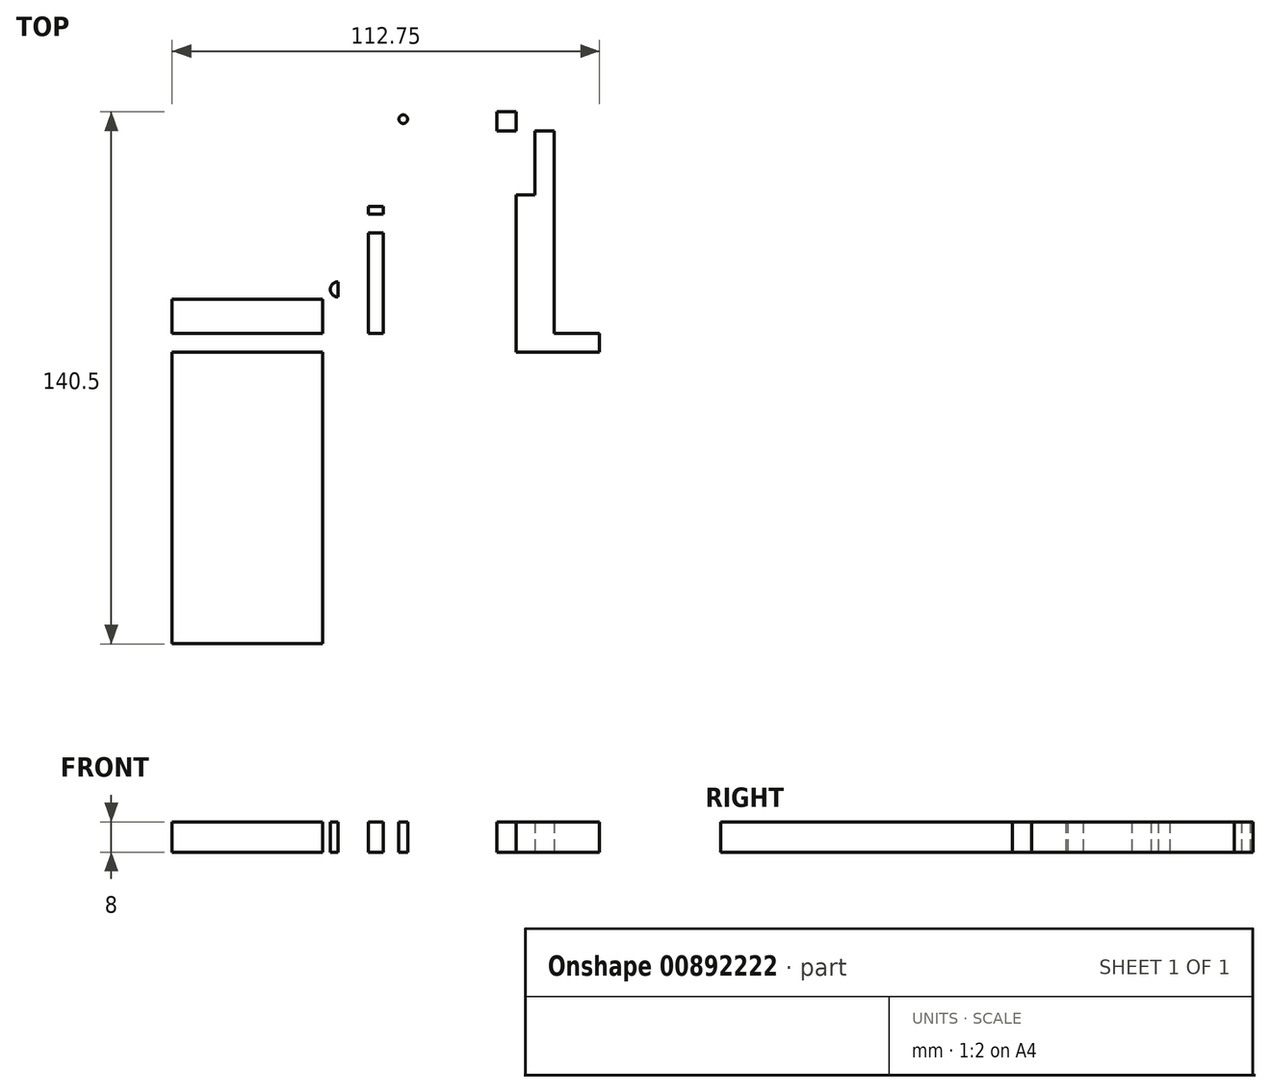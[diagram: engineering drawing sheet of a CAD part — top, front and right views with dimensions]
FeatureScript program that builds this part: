
annotation { "Feature Type Name" : "Feature", "Feature Type Description" : "" }
export const myFeature = defineFeature(function(context is Context, id is Id, definition is map)
    precondition{}
    {
        {
            var Q0;
            Q0=qCreatedBy(makeId("Top.planeOp"),FACE);
            var sketch = newSketch(context, id + "F0", { "sketchPlane" : qUnion([Q0])});
            skLineSegment(sketch, "E0.bottom", {"start": v(-40.7, -58.83) * mm, "end": v(14.3, -58.83) * mm});
            skLineSegment(sketch, "E0.top", {"start": v(-40.7, 44.67) * mm, "end": v(14.3, 44.67) * mm});
            skLineSegment(sketch, "E0.left", {"start": v(-40.7, -58.83) * mm, "end": v(-40.7, 44.67) * mm});
            skLineSegment(sketch, "E0.right", {"start": v(14.3, -58.83) * mm, "end": v(14.3, 44.67) * mm});
            skLineSegment(sketch, "E1.bottom", {"start": v(-45.7, 49.67) * mm, "end": v(85.3, 49.67) * mm});
            skLineSegment(sketch, "E1.top", {"start": v(-45.7, -150.83) * mm, "end": v(85.3, -150.83) * mm});
            skLineSegment(sketch, "E1.left", {"start": v(-45.7, 49.67) * mm, "end": v(-45.7, -150.83) * mm});
            skLineSegment(sketch, "E1.right", {"start": v(85.3, 49.67) * mm, "end": v(85.3, -150.83) * mm});
            skLineSegment(sketch, "E2.bottom", {"start": v(-40.7, -63.83) * mm, "end": v(80.3, -63.83) * mm});
            skLineSegment(sketch, "E2.top", {"start": v(-40.7, -145.83) * mm, "end": v(80.3, -145.83) * mm});
            skLineSegment(sketch, "E2.left", {"start": v(-40.7, -63.83) * mm, "end": v(-40.7, -145.83) * mm});
            skLineSegment(sketch, "E2.right", {"start": v(80.3, -63.83) * mm, "end": v(80.3, -145.83) * mm});
            skLineSegment(sketch, "E3.top", {"start": v(14.3, -63.83) * mm, "end": v(19.3, -63.83) * mm});
            skLineSegment(sketch, "E4.bottom", {"start": v(19.3, -58.83) * mm, "end": v(55.3, -58.83) * mm});
            skLineSegment(sketch, "E4.top", {"start": v(19.3, -32.33) * mm, "end": v(55.3, -32.33) * mm});
            skLineSegment(sketch, "E4.left", {"start": v(19.3, -58.83) * mm, "end": v(19.3, -32.33) * mm});
            skLineSegment(sketch, "E4.right", {"start": v(55.3, -58.83) * mm, "end": v(55.3, -32.33) * mm});
            skLineSegment(sketch, "E5.right", {"start": v(14.3, -32.33) * mm, "end": v(14.3, -27.33) * mm});
            skLineSegment(sketch, "E6.bottom", {"start": v(19.3, -27.33) * mm, "end": v(53.3, -27.33) * mm});
            skLineSegment(sketch, "E6.top", {"start": v(19.3, -0.33) * mm, "end": v(53.3, -0.33) * mm});
            skLineSegment(sketch, "E6.left", {"start": v(19.3, -27.33) * mm, "end": v(19.3, -0.33) * mm});
            skLineSegment(sketch, "E6.right", {"start": v(53.3, -27.33) * mm, "end": v(53.3, -0.33) * mm});
            skLineSegment(sketch, "E7", {"start": v(53.3, -27.33) * mm, "end": v(53.3, -22.33) * mm});
            skLineSegment(sketch, "E8", {"start": v(53.3, -22.33) * mm, "end": v(53.3, -5.33) * mm});
            skLineSegment(sketch, "E9.bottom", {"start": v(53.3, -5.33) * mm, "end": v(53.3, -5.33) * mm});
            skLineSegment(sketch, "E9.top", {"start": v(53.3, -22.33) * mm, "end": v(53.3, -22.33) * mm});
            skLineSegment(sketch, "E9.left", {"start": v(53.3, -5.33) * mm, "end": v(53.3, -22.33) * mm});
            skLineSegment(sketch, "E9.right", {"start": v(53.3, -5.33) * mm, "end": v(53.3, -22.33) * mm});
            skLineSegment(sketch, "E10.bottom", {"start": v(53.3, -22.33) * mm, "end": v(63.3, -22.33) * mm});
            skLineSegment(sketch, "E10.top", {"start": v(53.3, -5.33) * mm, "end": v(63.3, -5.33) * mm});
            skLineSegment(sketch, "E10.right", {"start": v(63.3, -22.33) * mm, "end": v(63.3, -5.33) * mm});
            skLineSegment(sketch, "E11.bottom", {"start": v(14.3, 44.67) * mm, "end": v(19.3, 44.67) * mm});
            skLineSegment(sketch, "E11.top", {"start": v(14.3, 49.67) * mm, "end": v(19.3, 49.67) * mm});
            skLineSegment(sketch, "E11.left", {"start": v(14.3, 44.67) * mm, "end": v(14.3, 49.67) * mm});
            skLineSegment(sketch, "E11.right", {"start": v(19.3, 44.67) * mm, "end": v(19.3, 49.67) * mm});
            skLineSegment(sketch, "E12.bottom", {"start": v(19.3, -0.33) * mm, "end": v(14.3, -0.33) * mm});
            skLineSegment(sketch, "E12.top", {"start": v(19.3, 4.67) * mm, "end": v(14.3, 4.67) * mm});
            skLineSegment(sketch, "E12.left", {"start": v(19.3, -0.33) * mm, "end": v(19.3, 4.67) * mm});
            skLineSegment(sketch, "E12.right", {"start": v(14.3, -0.33) * mm, "end": v(14.3, 4.67) * mm});
            skLineSegment(sketch, "E13.bottom", {"start": v(85.3, 49.67) * mm, "end": v(80.3, 49.67) * mm});
            skLineSegment(sketch, "E13.left", {"start": v(85.3, 49.67) * mm, "end": v(85.3, 44.67) * mm});
            skLineSegment(sketch, "E14.top", {"start": v(19.3, 49.67) * mm, "end": v(85.3, 49.67) * mm});
            skLineSegment(sketch, "E14.left", {"start": v(19.3, 4.67) * mm, "end": v(19.3, 49.67) * mm});
            skLineSegment(sketch, "E14.right", {"start": v(85.3, 4.67) * mm, "end": v(85.3, 49.67) * mm});
            skLineSegment(sketch, "E15.bottom", {"start": v(80.3, -63.83) * mm, "end": v(85.3, -63.83) * mm});
            skLineSegment(sketch, "E15.top", {"start": v(80.3, -58.83) * mm, "end": v(85.3, -58.83) * mm});
            skLineSegment(sketch, "E15.left", {"start": v(80.3, -63.83) * mm, "end": v(80.3, -58.83) * mm});
            skLineSegment(sketch, "E15.right", {"start": v(85.3, -63.83) * mm, "end": v(85.3, -58.83) * mm});
            skLineSegment(sketch, "E16", {"start": v(63.3, -5.33) * mm, "end": v(68.3, -5.33) * mm});
            skLineSegment(sketch, "E17", {"start": v(68.3, -5.33) * mm, "end": v(68.3, -22.33) * mm});
            skLineSegment(sketch, "E18.bottom", {"start": v(85.3, -58.83) * mm, "end": v(68.3, -58.83) * mm});
            skLineSegment(sketch, "E18.left", {"start": v(85.3, -58.83) * mm, "end": v(85.3, 4.67) * mm});
            skLineSegment(sketch, "E18.right", {"start": v(68.3, -58.83) * mm, "end": v(68.3, 4.67) * mm});
            skLineSegment(sketch, "E19", {"start": v(19.3, 4.67) * mm, "end": v(68.3, 4.67) * mm});
            skLineSegment(sketch, "E20.bottom", {"start": v(68.3, 4.67) * mm, "end": v(65.8, 4.67) * mm});
            skLineSegment(sketch, "E20.top", {"start": v(68.3, 2.17) * mm, "end": v(65.8, 2.17) * mm});
            skLineSegment(sketch, "E20.left", {"start": v(68.3, 4.67) * mm, "end": v(68.3, 2.17) * mm});
            skLineSegment(sketch, "E20.right", {"start": v(65.8, 4.67) * mm, "end": v(65.8, 2.17) * mm});
            skLineSegment(sketch, "E21.bottom", {"start": v(19.3, 44.67) * mm, "end": v(16.8, 44.67) * mm});
            skLineSegment(sketch, "E21.top", {"start": v(19.3, 47.17) * mm, "end": v(16.8, 47.17) * mm});
            skLineSegment(sketch, "E21.left", {"start": v(19.3, 44.67) * mm, "end": v(19.3, 47.17) * mm});
            skLineSegment(sketch, "E22.bottom", {"start": v(85.3, -58.83) * mm, "end": v(82.8, -58.83) * mm});
            skLineSegment(sketch, "E22.top", {"start": v(85.3, -61.33) * mm, "end": v(82.8, -61.33) * mm});
            skLineSegment(sketch, "E22.left", {"start": v(85.3, -58.83) * mm, "end": v(85.3, -61.33) * mm});
            skLineSegment(sketch, "E22.right", {"start": v(82.8, -58.83) * mm, "end": v(82.8, -61.33) * mm});
            skLineSegment(sketch, "E23.bottom", {"start": v(85.3, -150.83) * mm, "end": v(82.8, -150.83) * mm});
            skLineSegment(sketch, "E23.top", {"start": v(85.3, -148.33) * mm, "end": v(82.8, -148.33) * mm});
            skLineSegment(sketch, "E23.left", {"start": v(85.3, -150.83) * mm, "end": v(85.3, -148.33) * mm});
            skLineSegment(sketch, "E23.right", {"start": v(82.8, -150.83) * mm, "end": v(82.8, -148.33) * mm});
            skLineSegment(sketch, "E24.bottom", {"start": v(-45.7, -150.83) * mm, "end": v(-43.2, -150.83) * mm});
            skLineSegment(sketch, "E24.top", {"start": v(-45.7, -148.33) * mm, "end": v(-43.2, -148.33) * mm});
            skLineSegment(sketch, "E24.left", {"start": v(-45.7, -150.83) * mm, "end": v(-45.7, -148.33) * mm});
            skLineSegment(sketch, "E24.right", {"start": v(-43.2, -150.83) * mm, "end": v(-43.2, -148.33) * mm});
            skLineSegment(sketch, "E25.bottom", {"start": v(-45.7, 49.67) * mm, "end": v(-43.2, 49.67) * mm});
            skLineSegment(sketch, "E25.top", {"start": v(-45.7, 47.17) * mm, "end": v(-43.2, 47.17) * mm});
            skLineSegment(sketch, "E25.left", {"start": v(-45.7, 49.67) * mm, "end": v(-45.7, 47.17) * mm});
            skLineSegment(sketch, "E25.right", {"start": v(-43.2, 49.67) * mm, "end": v(-43.2, 47.17) * mm});
            skLineSegment(sketch, "E26.bottom", {"start": v(19.3, 49.67) * mm, "end": v(16.8, 49.67) * mm});
            skLineSegment(sketch, "E26.left", {"start": v(19.3, 49.67) * mm, "end": v(19.3, 47.17) * mm});
            skLineSegment(sketch, "E26.right", {"start": v(16.8, 49.67) * mm, "end": v(16.8, 47.17) * mm});
            skCircle(sketch, "E27", {"center": v(16.8, 47.17) * mm, "radius": 2 * mm});
            skCircle(sketch, "E28", {"center": v(65.8, 2.17) * mm, "radius": 2 * mm});
            skCircle(sketch, "E29", {"center": v(82.8, -61.33) * mm, "radius": 2 * mm});
            skCircle(sketch, "E30", {"center": v(82.8, -148.33) * mm, "radius": 2 * mm});
            skCircle(sketch, "E31", {"center": v(-43.2, -148.33) * mm, "radius": 2 * mm});
            skCircle(sketch, "E32", {"center": v(-43.2, 47.17) * mm, "radius": 2 * mm});
            skLineSegment(sketch, "E33.bottom", {"start": v(-40.7, -63.83) * mm, "end": v(-37.3, -63.83) * mm});
            skLineSegment(sketch, "E33.top", {"start": v(-40.7, -67.23) * mm, "end": v(-37.3, -67.23) * mm});
            skLineSegment(sketch, "E33.left", {"start": v(-40.7, -63.83) * mm, "end": v(-40.7, -67.23) * mm});
            skLineSegment(sketch, "E33.right", {"start": v(-37.3, -63.83) * mm, "end": v(-37.3, -67.23) * mm});
            skLineSegment(sketch, "E34.bottom", {"start": v(-40.7, -145.83) * mm, "end": v(-37.3, -145.83) * mm});
            skLineSegment(sketch, "E34.top", {"start": v(-40.7, -142.43) * mm, "end": v(-37.3, -142.43) * mm});
            skLineSegment(sketch, "E34.left", {"start": v(-40.7, -145.83) * mm, "end": v(-40.7, -142.43) * mm});
            skLineSegment(sketch, "E34.right", {"start": v(-37.3, -145.83) * mm, "end": v(-37.3, -142.43) * mm});
            skLineSegment(sketch, "E35.bottom", {"start": v(80.3, -145.83) * mm, "end": v(76.9, -145.83) * mm});
            skLineSegment(sketch, "E35.top", {"start": v(80.3, -142.43) * mm, "end": v(76.9, -142.43) * mm});
            skLineSegment(sketch, "E35.left", {"start": v(80.3, -145.83) * mm, "end": v(80.3, -142.43) * mm});
            skLineSegment(sketch, "E35.right", {"start": v(76.9, -145.83) * mm, "end": v(76.9, -142.43) * mm});
            skLineSegment(sketch, "E36.bottom", {"start": v(80.3, -63.83) * mm, "end": v(76.9, -63.83) * mm});
            skLineSegment(sketch, "E36.top", {"start": v(80.3, -67.23) * mm, "end": v(76.9, -67.23) * mm});
            skLineSegment(sketch, "E36.left", {"start": v(80.3, -63.83) * mm, "end": v(80.3, -67.23) * mm});
            skLineSegment(sketch, "E36.right", {"start": v(76.9, -63.83) * mm, "end": v(76.9, -67.23) * mm});
            skLineSegment(sketch, "E37.bottom", {"start": v(-40.7, -58.83) * mm, "end": v(-37.7, -58.83) * mm});
            skLineSegment(sketch, "E37.top", {"start": v(-40.7, 28.47) * mm, "end": v(-37.7, 28.47) * mm});
            skLineSegment(sketch, "E37.left", {"start": v(-40.7, -58.83) * mm, "end": v(-40.7, 28.47) * mm});
            skLineSegment(sketch, "E37.right", {"start": v(-37.7, -58.83) * mm, "end": v(-37.7, 28.47) * mm});
            skLineSegment(sketch, "E38.bottom", {"start": v(-37.7, -58.83) * mm, "end": v(-40.7, -58.83) * mm});
            skLineSegment(sketch, "E38.top", {"start": v(-37.7, -52.83) * mm, "end": v(-40.7, -52.83) * mm});
            skLineSegment(sketch, "E38.left", {"start": v(-37.7, -58.83) * mm, "end": v(-37.7, -52.83) * mm});
            skLineSegment(sketch, "E38.right", {"start": v(-40.7, -58.83) * mm, "end": v(-40.7, -52.83) * mm});
            skLineSegment(sketch, "E39.bottom", {"start": v(14.3, -58.83) * mm, "end": v(11.3, -58.83) * mm});
            skLineSegment(sketch, "E39.top", {"start": v(14.3, 29.87) * mm, "end": v(11.3, 29.87) * mm});
            skLineSegment(sketch, "E39.left", {"start": v(14.3, -58.83) * mm, "end": v(14.3, 29.87) * mm});
            skLineSegment(sketch, "E39.right", {"start": v(11.3, -58.83) * mm, "end": v(11.3, 29.87) * mm});
            skLineSegment(sketch, "E40.top", {"start": v(14.3, -47.23) * mm, "end": v(11.3, -47.23) * mm});
            skLineSegment(sketch, "E40.left", {"start": v(14.3, -58.83) * mm, "end": v(14.3, -47.23) * mm});
            skLineSegment(sketch, "E40.right", {"start": v(11.3, -58.83) * mm, "end": v(11.3, -47.23) * mm});
            skCircle(sketch, "E41", {"center": v(-37.7, -52.83) * mm, "radius": 2 * mm});
            skCircle(sketch, "E42", {"center": v(-37.7, 28.47) * mm, "radius": 2 * mm});
            skCircle(sketch, "E43", {"center": v(11.3, 29.87) * mm, "radius": 2 * mm});
            skCircle(sketch, "E44", {"center": v(11.3, -47.23) * mm, "radius": 2 * mm});
            skLineSegment(sketch, "E45.bottom", {"start": v(19.3, -0.33) * mm, "end": v(28.55, -0.33) * mm});
            skLineSegment(sketch, "E45.top", {"start": v(19.3, -2.28) * mm, "end": v(28.55, -2.28) * mm});
            skLineSegment(sketch, "E45.left", {"start": v(19.3, -0.33) * mm, "end": v(19.3, -2.28) * mm});
            skLineSegment(sketch, "E45.right", {"start": v(28.55, -0.33) * mm, "end": v(28.55, -2.28) * mm});
            skLineSegment(sketch, "E46.bottom", {"start": v(19.3, -27.33) * mm, "end": v(28.55, -27.33) * mm});
            skLineSegment(sketch, "E46.top", {"start": v(19.3, -25.38) * mm, "end": v(28.55, -25.38) * mm});
            skLineSegment(sketch, "E46.left", {"start": v(19.3, -27.33) * mm, "end": v(19.3, -25.38) * mm});
            skLineSegment(sketch, "E46.right", {"start": v(28.55, -27.33) * mm, "end": v(28.55, -25.38) * mm});
            skLineSegment(sketch, "E47.bottom", {"start": v(53.3, -0.33) * mm, "end": v(51.35, -0.33) * mm});
            skLineSegment(sketch, "E47.top", {"start": v(53.3, -2.28) * mm, "end": v(51.35, -2.28) * mm});
            skLineSegment(sketch, "E47.left", {"start": v(53.3, -0.33) * mm, "end": v(53.3, -2.28) * mm});
            skLineSegment(sketch, "E47.right", {"start": v(51.35, -0.33) * mm, "end": v(51.35, -2.28) * mm});
            skLineSegment(sketch, "E48.bottom", {"start": v(53.3, -27.33) * mm, "end": v(51.35, -27.33) * mm});
            skLineSegment(sketch, "E48.top", {"start": v(53.3, -25.38) * mm, "end": v(51.35, -25.38) * mm});
            skLineSegment(sketch, "E48.left", {"start": v(53.3, -27.33) * mm, "end": v(53.3, -25.38) * mm});
            skLineSegment(sketch, "E48.right", {"start": v(51.35, -27.33) * mm, "end": v(51.35, -25.38) * mm});
            skLineSegment(sketch, "E49.bottom", {"start": v(55.3, -32.33) * mm, "end": v(53.6, -32.33) * mm});
            skLineSegment(sketch, "E49.top", {"start": v(55.3, -34.03) * mm, "end": v(53.6, -34.03) * mm});
            skLineSegment(sketch, "E49.left", {"start": v(55.3, -32.33) * mm, "end": v(55.3, -34.03) * mm});
            skLineSegment(sketch, "E49.right", {"start": v(53.6, -32.33) * mm, "end": v(53.6, -34.03) * mm});
            skLineSegment(sketch, "E50.bottom", {"start": v(55.3, -58.83) * mm, "end": v(53.6, -58.83) * mm});
            skLineSegment(sketch, "E50.top", {"start": v(55.3, -57.13) * mm, "end": v(53.6, -57.13) * mm});
            skLineSegment(sketch, "E50.left", {"start": v(55.3, -58.83) * mm, "end": v(55.3, -57.13) * mm});
            skLineSegment(sketch, "E50.right", {"start": v(53.6, -58.83) * mm, "end": v(53.6, -57.13) * mm});
            skCircle(sketch, "E51", {"center": v(53.6, -34.03) * mm, "radius": 1.2 * mm});
            skCircle(sketch, "E52", {"center": v(53.6, -57.13) * mm, "radius": 1.2 * mm});
            skCircle(sketch, "E53", {"center": v(51.35, -25.38) * mm, "radius": 1.15 * mm});
            skCircle(sketch, "E54", {"center": v(28.55, -25.38) * mm, "radius": 1.15 * mm});
            skCircle(sketch, "E55", {"center": v(28.55, -2.28) * mm, "radius": 1.15 * mm});
            skCircle(sketch, "E56", {"center": v(51.35, -2.28) * mm, "radius": 1.15 * mm});
            skCircle(sketch, "E57", {"center": v(-37.3, -67.23) * mm, "radius": 1.4 * mm});
            skCircle(sketch, "E58", {"center": v(76.9, -67.23) * mm, "radius": 1.4 * mm});
            skCircle(sketch, "E59", {"center": v(-37.3, -142.43) * mm, "radius": 1.4 * mm});
            skCircle(sketch, "E60", {"center": v(76.9, -142.43) * mm, "radius": 1.4 * mm});
            skLineSegment(sketch, "E61.bottom", {"start": v(-40.7, -145.83) * mm, "end": v(-32.45, -145.83) * mm});
            skLineSegment(sketch, "E61.top", {"start": v(-40.7, -140.83) * mm, "end": v(-32.45, -140.83) * mm});
            skLineSegment(sketch, "E61.left", {"start": v(-40.7, -145.83) * mm, "end": v(-40.7, -140.83) * mm});
            skLineSegment(sketch, "E61.right", {"start": v(-32.45, -145.83) * mm, "end": v(-32.45, -140.83) * mm});
            skLineSegment(sketch, "E62.bottom", {"start": v(-40.7, -58.83) * mm, "end": v(-33.7, -58.83) * mm});
            skLineSegment(sketch, "E62.top", {"start": v(-40.7, -54.83) * mm, "end": v(-33.7, -54.83) * mm});
            skLineSegment(sketch, "E62.left", {"start": v(-40.7, -58.83) * mm, "end": v(-40.7, -54.83) * mm});
            skLineSegment(sketch, "E62.right", {"start": v(-33.7, -58.83) * mm, "end": v(-33.7, -54.83) * mm});
            skLineSegment(sketch, "E63", {"start": v(-33.7, -54.83) * mm, "end": v(-33.7, -49.83) * mm});
            skLineSegment(sketch, "E64", {"start": v(-33.7, -49.83) * mm, "end": v(-26.03, -49.83) * mm});
            skPoint(sketch, "E65.oppositeSnap0", {"position": v(-29.87, -49.83) * mm});
            skLineSegment(sketch, "E65.bottom", {"start": v(-32.45, -140.83) * mm, "end": v(-32.45, -140.83) * mm});
            skLineSegment(sketch, "E65.top", {"start": v(-32.45, -49.83) * mm, "end": v(-32.45, -49.83) * mm});
            skLineSegment(sketch, "E65.left", {"start": v(-32.45, -140.83) * mm, "end": v(-32.45, -49.83) * mm});
            skLineSegment(sketch, "E65.right", {"start": v(-32.45, -140.83) * mm, "end": v(-32.45, -49.83) * mm});
            skLineSegment(sketch, "E66.bottom", {"start": v(14.3, -58.83) * mm, "end": v(7.3, -58.83) * mm});
            skLineSegment(sketch, "E66.top", {"start": v(14.3, -49.83) * mm, "end": v(7.3, -49.83) * mm});
            skLineSegment(sketch, "E66.left", {"start": v(14.3, -58.83) * mm, "end": v(14.3, -49.83) * mm});
            skLineSegment(sketch, "E66.right", {"start": v(7.3, -58.83) * mm, "end": v(7.3, -49.83) * mm});
            skLineSegment(sketch, "E67.bottom", {"start": v(-32.45, -140.83) * mm, "end": v(7.3, -140.83) * mm});
            skLineSegment(sketch, "E67.top", {"start": v(-32.45, -49.83) * mm, "end": v(7.3, -49.83) * mm});
            skLineSegment(sketch, "E67.right", {"start": v(7.3, -140.83) * mm, "end": v(7.3, -49.83) * mm});
            skLineSegment(sketch, "E68.bottom", {"start": v(19.3, -0.33) * mm, "end": v(23.3, -0.33) * mm});
            skLineSegment(sketch, "E68.top", {"start": v(19.3, -27.33) * mm, "end": v(23.3, -27.33) * mm});
            skLineSegment(sketch, "E68.left", {"start": v(19.3, -0.33) * mm, "end": v(19.3, -27.33) * mm});
            skLineSegment(sketch, "E68.right", {"start": v(23.3, -0.33) * mm, "end": v(23.3, -27.33) * mm});
            skLineSegment(sketch, "E69.bottom", {"start": v(19.3, -32.33) * mm, "end": v(23.3, -32.33) * mm});
            skLineSegment(sketch, "E69.top", {"start": v(19.3, -58.83) * mm, "end": v(23.3, -58.83) * mm});
            skLineSegment(sketch, "E69.left", {"start": v(19.3, -32.33) * mm, "end": v(19.3, -58.83) * mm});
            skLineSegment(sketch, "E69.right", {"start": v(23.3, -32.33) * mm, "end": v(23.3, -58.83) * mm});
            skLineSegment(sketch, "E70.bottom", {"start": v(23.3, -0.33) * mm, "end": v(-32.45, -0.33) * mm});
            skLineSegment(sketch, "E70.top", {"start": v(23.3, -58.83) * mm, "end": v(-32.45, -58.83) * mm});
            skLineSegment(sketch, "E70.left", {"start": v(23.3, -0.33) * mm, "end": v(23.3, -58.83) * mm});
            skLineSegment(sketch, "E70.right", {"start": v(-32.45, -0.33) * mm, "end": v(-32.45, -58.83) * mm});
            skLineSegment(sketch, "E71", {"start": v(68.3, 4.67) * mm, "end": v(58.3, 4.67) * mm});
            skLineSegment(sketch, "E72", {"start": v(58.3, 4.67) * mm, "end": v(58.3, -63.83) * mm});
            skLineSegment(sketch, "E73", {"start": v(53.3, -0.33) * mm, "end": v(58.3, -0.33) * mm});
            skSolve(sketch);
        }
        {
            var Q0;
            {var subQ5=sQuery(id+"F0.wireOp",EDGE,"E67.bottom");Q0=makeQuery(id+"F0.imprint","IMPRINT",FACE,{"disambiguationData":[TD([[makeQuery(id+"F0.imprint","IMPRINT",EDGE,{"derivedFrom":subQ5}),1.0]])]});}
            var Q1;
            {var subQ0=sQuery(id+"F0.wireOp",EDGE,"E65.left");var subQ1=sQuery(id+"F0.wireOp",EDGE,"E2.bottom");var subQ2=makeQuery(id+"F0.imprint","INTERSECT",VERTEX,{"derivedFrom":[subQ1,subQ0]});Q1=makeQuery(id+"F0.imprint","IMPRINT",FACE,{"disambiguationData":[TD([[makeQuery(id+"F0.imprint","IMPRINT",EDGE,{"disambiguationData":[TD([[subQ2,-1.0]])],"derivedFrom":subQ1}),1.0]])]});}
            var Q2;
            {var subQ5=sQuery(id+"F0.wireOp",EDGE,"E67.top");var subQ8=makeQuery(id+"F0.imprint","IMPRINT",VERTEX,{"derivedFrom":subQ5});Q2=makeQuery(id+"F0.imprint","IMPRINT",FACE,{"disambiguationData":[TD([[makeQuery(id+"F0.imprint","IMPRINT",EDGE,{"disambiguationData":[TD([[subQ8,1.0]])],"derivedFrom":subQ5}),-1.0]])]});}
            var Q3;
            {var subQ0=sQuery(id+"F0.wireOp",EDGE,"E44");var subQ1=sQuery(id+"F0.wireOp",EDGE,"E39.right");var subQ2=makeQuery(id+"F0.imprint","INTERSECT",VERTEX,{"derivedFrom":[subQ1,subQ0]});Q3=makeQuery(id+"F0.imprint","IMPRINT",FACE,{"disambiguationData":[TD([[makeQuery(id+"F0.imprint","IMPRINT",EDGE,{"disambiguationData":[TD([[subQ2,-1.0]])],"derivedFrom":subQ1}),1.0]])]});}
            var Q4;
            {var subQ0=sQuery(id+"F0.wireOp",EDGE,"E70.top");var subQ1=sQuery(id+"F0.wireOp",EDGE,"E40.right");var subQ2=makeQuery(id+"F0.imprint","INTERSECT",VERTEX,{"derivedFrom":[subQ1,subQ0]});Q4=makeQuery(id+"F0.imprint","IMPRINT",FACE,{"disambiguationData":[TD([[makeQuery(id+"F0.imprint","IMPRINT",EDGE,{"disambiguationData":[TD([[subQ2,-1.0]])],"derivedFrom":subQ1}),1.0]])]});}
            var Q5;
            {var subQ5=sQuery(id+"F0.wireOp",EDGE,"E66.left");Q5=makeQuery(id+"F0.imprint","IMPRINT",FACE,{"disambiguationData":[TD([[makeQuery(id+"F0.imprint","IMPRINT",EDGE,{"derivedFrom":subQ5}),1.0]])]});}
            var Q6;
            {var subQ11=sQuery(id+"F0.wireOp",EDGE,"E40.left");Q6=makeQuery(id+"F0.imprint","IMPRINT",FACE,{"disambiguationData":[TD([[makeQuery(id+"F0.imprint","IMPRINT",EDGE,{"derivedFrom":subQ11}),-1.0]])]});}
            var Q7;
            {var subQ0=sQuery(id+"F0.wireOp",EDGE,"E69.bottom");Q7=makeQuery(id+"F0.imprint","IMPRINT",FACE,{"disambiguationData":[TD([[makeQuery(id+"F0.imprint","IMPRINT",EDGE,{"derivedFrom":subQ0}),-1.0]])]});}
            var Q8;
            {var subQ0=sQuery(id+"F0.wireOp",EDGE,"E39.left");var subQ8=makeQuery(id+"F0.imprint","IMPRINT",VERTEX,{"disambiguationData":[OD(0.0)],"derivedFrom":subQ0});Q8=makeQuery(id+"F0.imprint","IMPRINT",FACE,{"disambiguationData":[TD([[makeQuery(id+"F0.imprint","IMPRINT",EDGE,{"disambiguationData":[TD([[subQ8,-1.0]])],"derivedFrom":subQ0}),1.0]])]});}
            var Q9;
            {var subQ0=sQuery(id+"F0.wireOp",EDGE,"E68.left");var subQ1=sQuery(id+"F0.wireOp",EDGE,"E45.top");var subQ2=makeQuery(id+"F0.imprint","INTERSECT",VERTEX,{"derivedFrom":[subQ1,subQ0]});Q9=makeQuery(id+"F0.imprint","IMPRINT",FACE,{"disambiguationData":[TD([[makeQuery(id+"F0.imprint","IMPRINT",EDGE,{"disambiguationData":[TD([[subQ2,-1.0]])],"derivedFrom":subQ1}),-1.0]])]});}
            var Q10;
            {var subQ5=sQuery(id+"F0.wireOp",EDGE,"E68.top");Q10=makeQuery(id+"F0.imprint","IMPRINT",FACE,{"disambiguationData":[TD([[makeQuery(id+"F0.imprint","IMPRINT",EDGE,{"derivedFrom":subQ5}),1.0]])]});}
            var Q11;
            {var subQ0=sQuery(id+"F0.wireOp",EDGE,"E68.left");var subQ1=sQuery(id+"F0.wireOp",EDGE,"E45.top");var subQ2=makeQuery(id+"F0.imprint","INTERSECT",VERTEX,{"derivedFrom":[subQ1,subQ0]});Q11=makeQuery(id+"F0.imprint","IMPRINT",FACE,{"disambiguationData":[TD([[makeQuery(id+"F0.imprint","IMPRINT",EDGE,{"disambiguationData":[TD([[subQ2,-1.0]])],"derivedFrom":subQ1}),1.0]])]});}
            var Q12;
            {var subQ7=sQuery(id+"F0.wireOp",EDGE,"E40.left");Q12=makeQuery(id+"F0.imprint","IMPRINT",FACE,{"disambiguationData":[TD([[makeQuery(id+"F0.imprint","IMPRINT",EDGE,{"derivedFrom":subQ7}),1.0]])]});}
            var Q13;
            {var subQ12=sQuery(id+"F0.wireOp",EDGE,"E4.bottom");Q13=makeQuery(id+"F0.imprint","IMPRINT",FACE,{"disambiguationData":[TD([[makeQuery(id+"F0.imprint","IMPRINT",EDGE,{"derivedFrom":subQ12}),1.0]])]});}
            var Q14;
            {var subQ1=sQuery(id+"F0.wireOp",EDGE,"E6.bottom");Q14=makeQuery(id+"F0.imprint","IMPRINT",FACE,{"disambiguationData":[TD([[makeQuery(id+"F0.imprint","IMPRINT",EDGE,{"derivedFrom":subQ1}),1.0]])]});}
            var Q15;
            {var subQ5=sQuery(id+"F0.wireOp",EDGE,"E46.bottom");Q15=makeQuery(id+"F0.imprint","IMPRINT",FACE,{"disambiguationData":[TD([[makeQuery(id+"F0.imprint","IMPRINT",EDGE,{"derivedFrom":subQ5}),1.0]])]});}
            var Q16;
            {var subQ1=sQuery(id+"F0.wireOp",EDGE,"E49.bottom");Q16=makeQuery(id+"F0.imprint","IMPRINT",FACE,{"disambiguationData":[TD([[makeQuery(id+"F0.imprint","IMPRINT",EDGE,{"derivedFrom":subQ1}),1.0]])]});}
            var Q17;
            {var subQ1=sQuery(id+"F0.wireOp",EDGE,"E48.bottom");Q17=makeQuery(id+"F0.imprint","IMPRINT",FACE,{"disambiguationData":[TD([[makeQuery(id+"F0.imprint","IMPRINT",EDGE,{"derivedFrom":subQ1}),-1.0]])]});}
            var Q18;
            {var subQ1=sQuery(id+"F0.wireOp",EDGE,"E50.bottom");Q18=makeQuery(id+"F0.imprint","IMPRINT",FACE,{"disambiguationData":[TD([[makeQuery(id+"F0.imprint","IMPRINT",EDGE,{"derivedFrom":subQ1}),-1.0]])]});}
            var Q19;
            {var subQ5=sQuery(id+"F0.wireOp",EDGE,"E45.bottom");Q19=makeQuery(id+"F0.imprint","IMPRINT",FACE,{"disambiguationData":[TD([[makeQuery(id+"F0.imprint","IMPRINT",EDGE,{"derivedFrom":subQ5}),-1.0]])]});}
            var Q20;
            {var subQ1=sQuery(id+"F0.wireOp",EDGE,"E47.bottom");Q20=makeQuery(id+"F0.imprint","IMPRINT",FACE,{"disambiguationData":[TD([[makeQuery(id+"F0.imprint","IMPRINT",EDGE,{"derivedFrom":subQ1}),1.0]])]});}
            var Q21;
            {var subQ11=sQuery(id+"F0.wireOp",EDGE,"E3.top");Q21=makeQuery(id+"F0.imprint","IMPRINT",FACE,{"disambiguationData":[TD([[makeQuery(id+"F0.imprint","IMPRINT",EDGE,{"derivedFrom":subQ11}),1.0]])]});}
            var Q22;
            {var subQ0=sQuery(id+"F0.wireOp",EDGE,"E8");Q22=makeQuery(id+"F0.imprint","IMPRINT",FACE,{"disambiguationData":[TD([[makeQuery(id+"F0.imprint","IMPRINT",EDGE,{"derivedFrom":subQ0}),-1.0]])]});}
            var Q23;
            {var subQ4=sQuery(id+"F0.wireOp",EDGE,"E6.right");Q23=makeQuery(id+"F0.imprint","IMPRINT",FACE,{"disambiguationData":[TD([[makeQuery(id+"F0.imprint","IMPRINT",EDGE,{"derivedFrom":subQ4}),-1.0]])]});}
            extrude(context, id + "F1", {"entities" : qUnion([Q0, Q1, Q2, Q3, Q4, Q5, Q6, Q7, Q8, Q9, Q10, Q11, Q12, Q13, Q14, Q15, Q16, Q17, Q18, Q19, Q20, Q21, Q22, Q23]), "depth" : 8 * mm, "offsetDistance" : 25 * mm});
        }
    });
